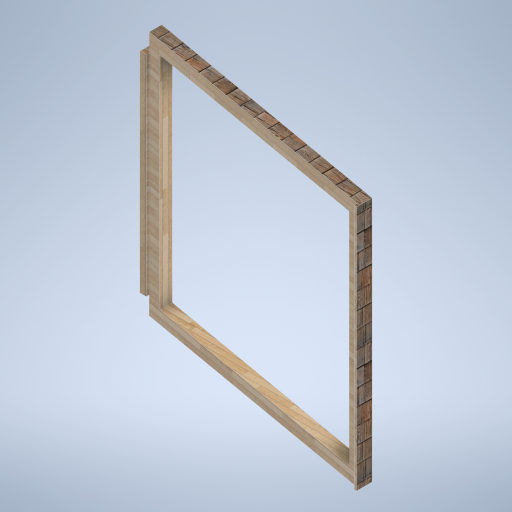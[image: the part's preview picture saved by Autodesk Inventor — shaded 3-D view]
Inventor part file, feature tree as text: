
AUTODESK INVENTOR PART (.ipt)
format: ipt  version: 2024.2 (Build 282272000, 272)  size: 364,544 bytes
history: native  units: in
note: dims shown in document units (in); Inventor stores cm internally (conversion verified against a paired STEP export)
features: sketch x9, plane x4, other x3
ambient origin geometry x8: Origin, YZ Plane, XZ Plane, XY Plane, X Axis, Y Axis, Z Axis, Center Point
bodies: Solid1 (feature_tree)
feature tree (16):
  other  "eave_frame_side.ipt"
  other  "Solid1::eave_frame_side.ipt"
  other  "TaggingFeature1"
  sketch  "Sketch1"  dims[d0=0.3937in]
  sketch  "Sketch2"
  sketch  "Sketch3"
  sketch  "Sketch4"
  sketch  "Sketch5"
  sketch  "Sketch6"
  sketch  "Sketch7"
  sketch  "Sketch8"
  sketch  "Sketch9"
  plane  "Work Plane1"
  plane  "Work Plane2"
  plane  "Work Plane3"
  plane  "Work Plane4"
